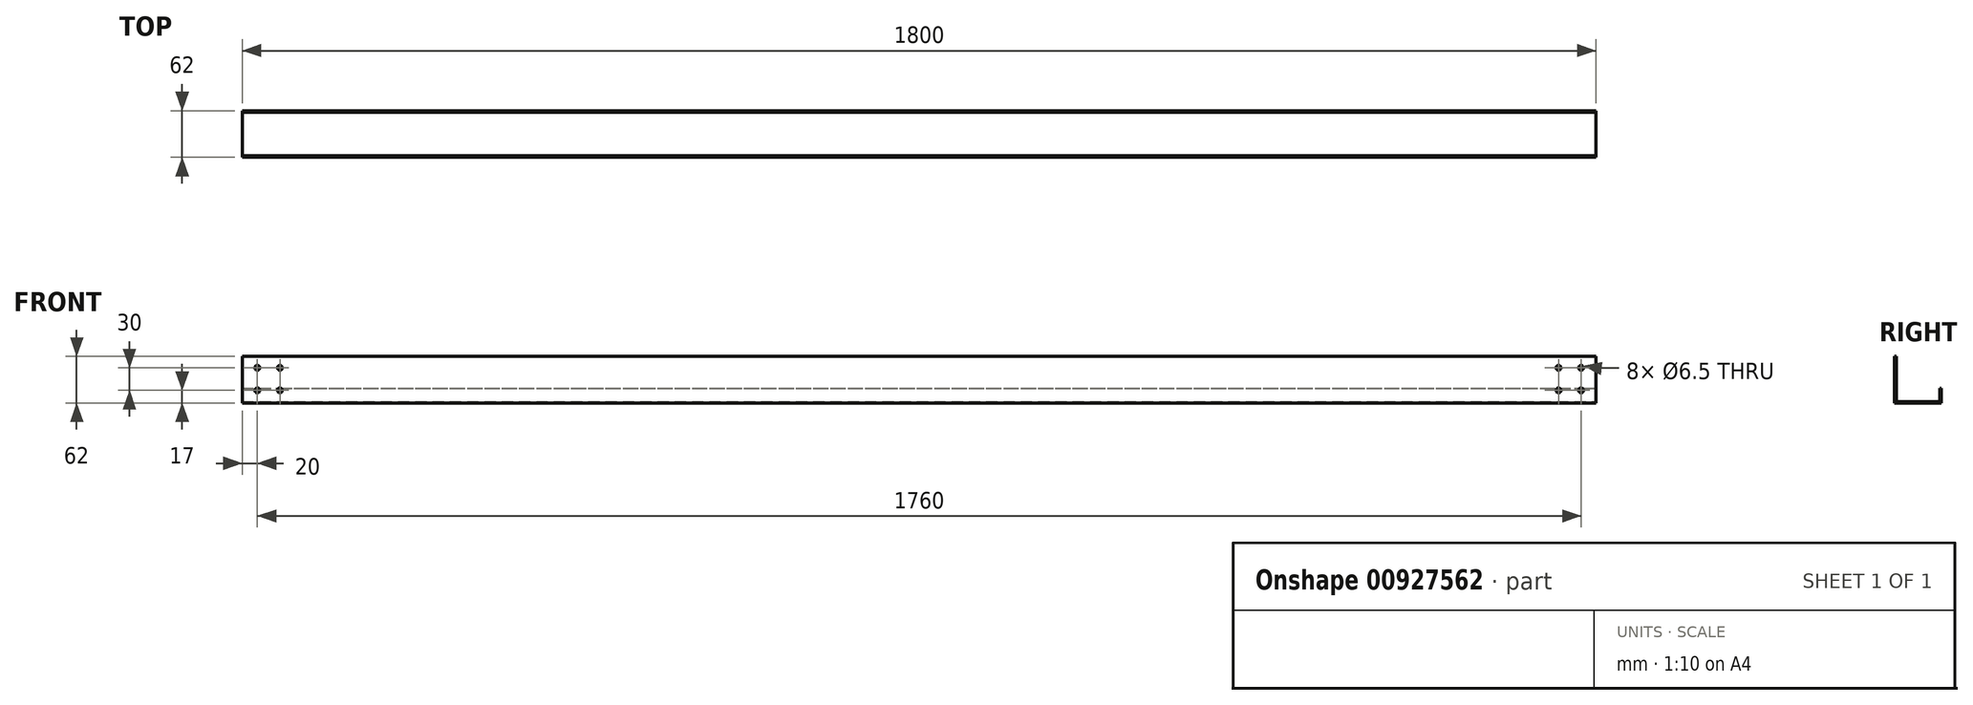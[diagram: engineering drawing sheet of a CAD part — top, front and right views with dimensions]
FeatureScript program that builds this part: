
annotation { "Feature Type Name" : "Feature", "Feature Type Description" : "" }
export const myFeature = defineFeature(function(context is Context, id is Id, definition is map)
    precondition{}
    {
        {
            var Q0;
            Q0=qCreatedBy(makeId("Right.planeOp"),FACE);
            var sketch = newSketch(context, id + "F0", { "sketchPlane" : qUnion([Q0])});
            skLineSegment(sketch, "E0", {"start": v(0, 0) * mm, "end": v(62, 0) * mm});
            skLineSegment(sketch, "E1", {"start": v(0, 0) * mm, "end": v(0, 62) * mm});
            skLineSegment(sketch, "E2.0", {"start": v(2, 2) * mm, "end": v(2, 62) * mm});
            skLineSegment(sketch, "E2.1", {"start": v(2, 2) * mm, "end": v(60, 2) * mm});
            skLineSegment(sketch, "E3", {"start": v(0, 62) * mm, "end": v(2, 62) * mm});
            skLineSegment(sketch, "E4", {"start": v(60, 2) * mm, "end": v(60, 20) * mm});
            skLineSegment(sketch, "E5.0", {"start": v(62, 0) * mm, "end": v(62, 20) * mm});
            skLineSegment(sketch, "E6", {"start": v(62, 20) * mm, "end": v(60, 20) * mm});
            skSolve(sketch);
        }
        {
            var Q0;
            Q0 = qSketchRegion(id + "F0", true);
            extrude(context, id + "F1", {"entities" : qUnion([Q0]), "oppositeDirection" : true, "depth" : 1800 * mm, "offsetDistance" : 25 * mm});
        }
        {
            var Q0;
            Q0=makeQuery(id+"F1.opExtrude","SWEPT_FACE",FACE,{"disambiguationData":[OSD([sQuery(id+"F0.wireOp",EDGE,"E2.0")])]});
            var sketch = newSketch(context, id + "F2", { "sketchPlane" : qUnion([Q0])});
            skLineSegment(sketch, "E7", {"start": v(-589.17, 32) * mm, "end": v(2575.81, 32) * mm, "construction": true});
            skCircle(sketch, "E8", {"center": v(20, 47) * mm, "radius": 3.25 * mm});
            skCircle(sketch, "E9", {"center": v(50, 47) * mm, "radius": 3.25 * mm});
            skCircle(sketch, "E10.MirrorC", {"center": v(20, 17) * mm, "radius": 3.25 * mm});
            skCircle(sketch, "E11.MirrorC", {"center": v(50, 17) * mm, "radius": 3.25 * mm});
            skLineSegment(sketch, "E12", {"start": v(900, -419.47) * mm, "end": v(900, 408.62) * mm, "construction": true});
            skCircle(sketch, "E13.MirrorC", {"center": v(1750, 47) * mm, "radius": 3.25 * mm});
            skCircle(sketch, "E14.MirrorC", {"center": v(1780, 47) * mm, "radius": 3.25 * mm});
            skCircle(sketch, "E15.MirrorC", {"center": v(1780, 17) * mm, "radius": 3.25 * mm});
            skCircle(sketch, "E16.MirrorC", {"center": v(1750, 17) * mm, "radius": 3.25 * mm});
            skSolve(sketch);
        }
        {
            var Q0;
            Q0 = qSketchRegion(id + "F2", true);
            extrude(context, id + "F3", {"entities" : qUnion([Q0]), "operationType" : NewBodyOperationType.REMOVE, "oppositeDirection" : true, "depth" : 25 * mm, "offsetDistance" : 25 * mm});
        }
    });
